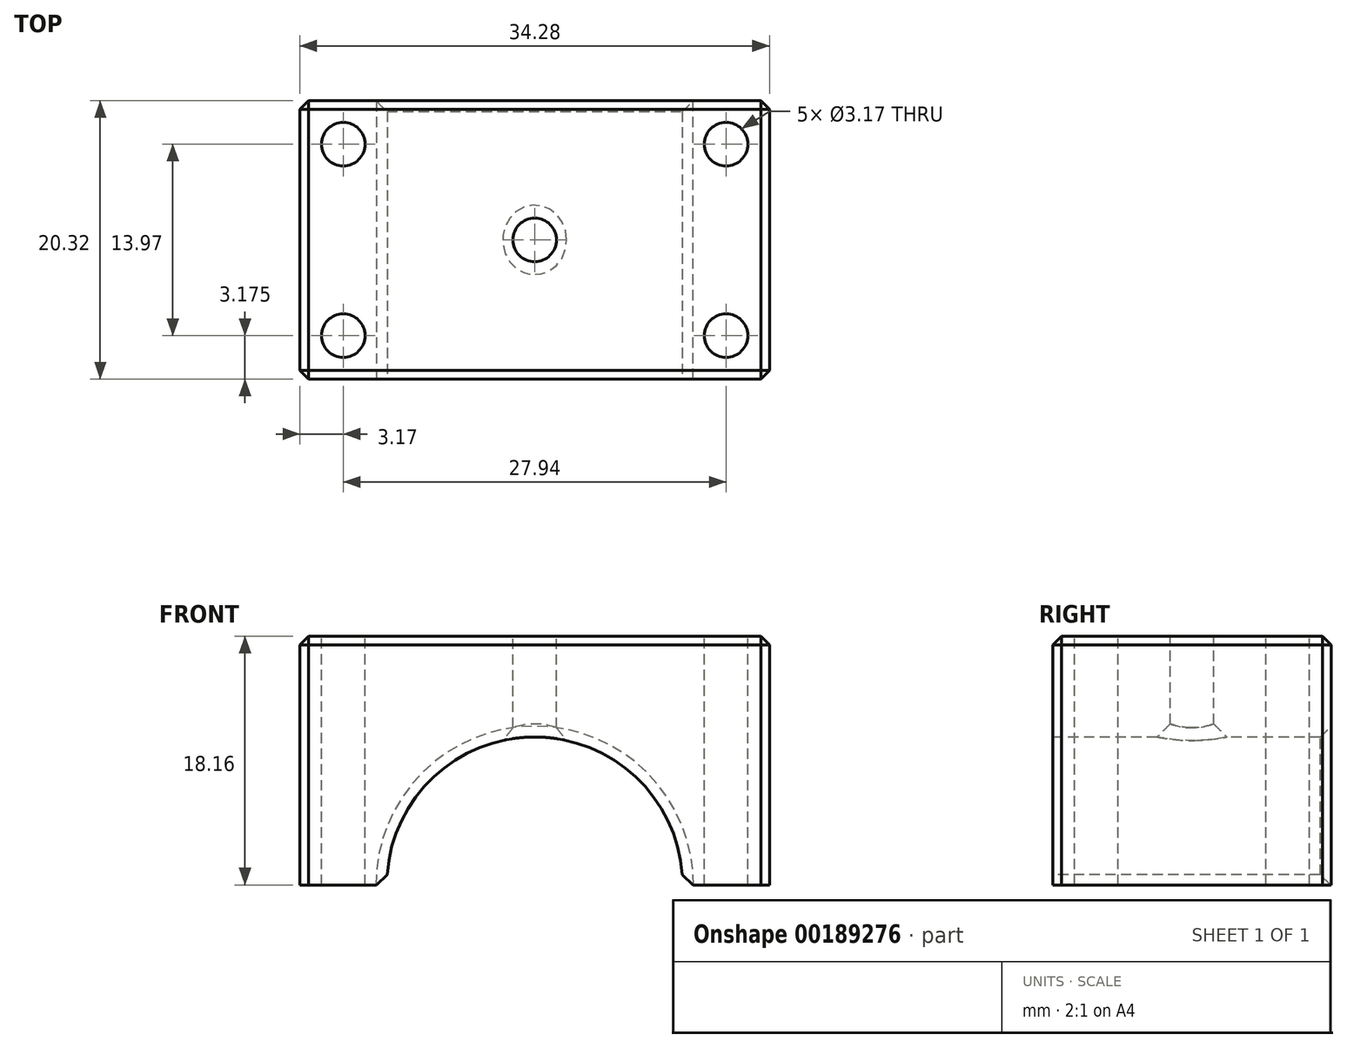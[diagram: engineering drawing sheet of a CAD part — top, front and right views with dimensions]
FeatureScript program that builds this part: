
annotation { "Feature Type Name" : "Feature", "Feature Type Description" : "" }
export const myFeature = defineFeature(function(context is Context, id is Id, definition is map)
    precondition{}
    {
        {
            var Q0;
            Q0=qCreatedBy(makeId("Top.planeOp"),FACE);
            var sketch = newSketch(context, id + "F0", { "sketchPlane" : qUnion([Q0])});
            skLineSegment(sketch, "E0", {"start": v(0, 0) * mm, "end": v(-17.15, 0) * mm});
            skLineSegment(sketch, "E1", {"start": v(-17.15, 0) * mm, "end": v(-17.15, 10.16) * mm});
            skLineSegment(sketch, "E2", {"start": v(-17.15, 10.16) * mm, "end": v(0, 10.16) * mm});
            skLineSegment(sketch, "E3", {"start": v(0, 10.16) * mm, "end": v(0, 0) * mm});
            skLineSegment(sketch, "E4.MirrorCS", {"start": v(17.15, 10.16) * mm, "end": v(0, 10.16) * mm});
            skLineSegment(sketch, "E5.MirrorCS", {"start": v(17.15, 0) * mm, "end": v(17.15, 10.16) * mm});
            skLineSegment(sketch, "E6.MirrorCS", {"start": v(0, 0) * mm, "end": v(17.15, 0) * mm});
            skLineSegment(sketch, "E7.MirrorCS", {"start": v(-17.15, 0) * mm, "end": v(-17.15, -10.16) * mm});
            skLineSegment(sketch, "E8.MirrorCS", {"start": v(-17.15, -10.16) * mm, "end": v(0, -10.16) * mm});
            skLineSegment(sketch, "E9.MirrorCS", {"start": v(17.15, -10.16) * mm, "end": v(0, -10.16) * mm});
            skLineSegment(sketch, "E10.MirrorCS", {"start": v(17.15, 0) * mm, "end": v(17.15, -10.16) * mm});
            skSolve(sketch);
        }
        {
            var Q0;
            Q0 = qSketchRegion(id + "F0", true);
            extrude(context, id + "F1", {"entities" : qUnion([Q0]), "depth" : 18.16 * mm});
        }
        {
            var Q0;
            Q0=makeQuery(id+"F1.opExtrude","SWEPT_FACE",FACE,{"disambiguationData":[OSD([sQuery(id+"F0.wireOp",EDGE,"E8.MirrorCS"),sQuery(id+"F0.wireOp",EDGE,"E9.MirrorCS")])]});
            var sketch = newSketch(context, id + "F2", { "sketchPlane" : qUnion([Q0])});
            skCircle(sketch, "E11", {"center": v(0, 0) * mm, "radius": 10.8 * mm});
            skSolve(sketch);
        }
        {
            var Q0;
            Q0 = qSketchRegion(id + "F2", true);
            extrude(context, id + "F3", {"entities" : qUnion([Q0]), "operationType" : NewBodyOperationType.REMOVE, "oppositeDirection" : true, "depth" : 38.1 * mm});
        }
        {
            var Q0;
            Q0=makeQuery(id+"F1.opExtrude","CAP_FACE",FACE,{"disambiguationData":[OSD([sQuery(id+"F0.wireOp",EDGE,"E1"),sQuery(id+"F0.wireOp",EDGE,"E2"),sQuery(id+"F0.wireOp",EDGE,"E4.MirrorCS"),sQuery(id+"F0.wireOp",EDGE,"E5.MirrorCS"),sQuery(id+"F0.wireOp",EDGE,"E7.MirrorCS"),sQuery(id+"F0.wireOp",EDGE,"E8.MirrorCS"),sQuery(id+"F0.wireOp",EDGE,"E9.MirrorCS"),sQuery(id+"F0.wireOp",EDGE,"E10.MirrorCS")])],"isStart":false});
            var sketch = newSketch(context, id + "F4", { "sketchPlane" : qUnion([Q0])});
            skCircle(sketch, "E12", {"center": v(0, 0) * mm, "radius": 1.59 * mm});
            skCircle(sketch, "E13", {"center": v(13.97, 6.99) * mm, "radius": 1.59 * mm});
            skCircle(sketch, "E14.MirrorC", {"center": v(13.97, -6.99) * mm, "radius": 1.59 * mm});
            skCircle(sketch, "E15.MirrorC", {"center": v(-13.97, 6.99) * mm, "radius": 1.59 * mm});
            skCircle(sketch, "E16.MirrorC", {"center": v(-13.97, -6.99) * mm, "radius": 1.59 * mm});
            skSolve(sketch);
        }
        {
            var Q0;
            Q0 = qSketchRegion(id + "F4", true);
            extrude(context, id + "F5", {"entities" : qUnion([Q0]), "operationType" : NewBodyOperationType.REMOVE, "oppositeDirection" : true, "depth" : 25.4 * mm});
        }
        {
            var Q0;
            Q0=makeQuery(id+"F5.boolean.opBoolean","INTERSECT",EDGE,{"derivedFrom":[makeQuery(id+"F3.boolean.opBoolean","COPY",FACE,{"derivedFrom":makeQuery(id+"F3.opExtrude","SWEPT_FACE",FACE,{"disambiguationData":[OSD([sQuery(id+"F2.wireOp",EDGE,"E11")])]})}),makeQuery(id+"F5.opExtrude","SWEPT_FACE",FACE,{"disambiguationData":[OSD([sQuery(id+"F4.wireOp",EDGE,"E12")])]})]});
            chamfer(context, id + "F6", {"entities" : qUnion([Q0]), "width" : 0.95 * mm, "tangentPropagation" : true});
        }
        {
            var Q0;
            Q0=makeQuery(id+"F3.boolean.opBoolean","INTERSECT",EDGE,{"disambiguationData":[OD(0.0)],"derivedFrom":[makeQuery(id+"F1.opExtrude","CAP_FACE",FACE,{"disambiguationData":[OSD([sQuery(id+"F0.wireOp",EDGE,"E1"),sQuery(id+"F0.wireOp",EDGE,"E2"),sQuery(id+"F0.wireOp",EDGE,"E4.MirrorCS"),sQuery(id+"F0.wireOp",EDGE,"E5.MirrorCS"),sQuery(id+"F0.wireOp",EDGE,"E7.MirrorCS"),sQuery(id+"F0.wireOp",EDGE,"E8.MirrorCS"),sQuery(id+"F0.wireOp",EDGE,"E9.MirrorCS"),sQuery(id+"F0.wireOp",EDGE,"E10.MirrorCS")])],"isStart":true}),makeQuery(id+"F3.opExtrude","SWEPT_FACE",FACE,{"disambiguationData":[OSD([sQuery(id+"F2.wireOp",EDGE,"E11")])]})]});
            var Q1;
            Q1=makeQuery(id+"F3.boolean.opBoolean","INTERSECT",EDGE,{"derivedFrom":[makeQuery(id+"F1.opExtrude","SWEPT_FACE",FACE,{"disambiguationData":[OSD([sQuery(id+"F0.wireOp",EDGE,"E2"),sQuery(id+"F0.wireOp",EDGE,"E4.MirrorCS")])]}),makeQuery(id+"F3.opExtrude","SWEPT_FACE",FACE,{"disambiguationData":[OSD([sQuery(id+"F2.wireOp",EDGE,"E11")])]})]});
            var Q2;
            Q2=makeQuery(id+"F3.boolean.opBoolean","INTERSECT",EDGE,{"disambiguationData":[OD(1.0)],"derivedFrom":[makeQuery(id+"F1.opExtrude","CAP_FACE",FACE,{"disambiguationData":[OSD([sQuery(id+"F0.wireOp",EDGE,"E1"),sQuery(id+"F0.wireOp",EDGE,"E2"),sQuery(id+"F0.wireOp",EDGE,"E4.MirrorCS"),sQuery(id+"F0.wireOp",EDGE,"E5.MirrorCS"),sQuery(id+"F0.wireOp",EDGE,"E7.MirrorCS"),sQuery(id+"F0.wireOp",EDGE,"E8.MirrorCS"),sQuery(id+"F0.wireOp",EDGE,"E9.MirrorCS"),sQuery(id+"F0.wireOp",EDGE,"E10.MirrorCS")])],"isStart":true}),makeQuery(id+"F3.opExtrude","SWEPT_FACE",FACE,{"disambiguationData":[OSD([sQuery(id+"F2.wireOp",EDGE,"E11")])]})]});
            var Q3;
            Q3=makeQuery(id+"F3.boolean.opBoolean","COPY",EDGE,{"derivedFrom":makeQuery(id+"F3.opExtrude","CAP_EDGE",EDGE,{"disambiguationData":[OSD([sQuery(id+"F2.wireOp",EDGE,"E11")])],"isStart":true})});
            chamfer(context, id + "F7", {"entities" : qUnion([Q0, Q1, Q2, Q3]), "width" : 0.8 * mm, "tangentPropagation" : true});
        }
        {
            var Q0;
            Q0=makeQuery(id+"F1.opExtrude","SWEPT_EDGE",EDGE,{"disambiguationData":[OSD([sQuery(id+"F0.wireOp",EDGE,"E9.MirrorCS"),sQuery(id+"F0.wireOp",EDGE,"E10.MirrorCS")])]});
            var Q1;
            Q1=makeQuery(id+"F1.opExtrude","SWEPT_EDGE",EDGE,{"disambiguationData":[OSD([sQuery(id+"F0.wireOp",EDGE,"E7.MirrorCS"),sQuery(id+"F0.wireOp",EDGE,"E8.MirrorCS")])]});
            var Q2;
            Q2=makeQuery(id+"F1.opExtrude","SWEPT_EDGE",EDGE,{"disambiguationData":[OSD([sQuery(id+"F0.wireOp",EDGE,"E1"),sQuery(id+"F0.wireOp",EDGE,"E2")])]});
            var Q3;
            Q3=makeQuery(id+"F1.opExtrude","SWEPT_EDGE",EDGE,{"disambiguationData":[OSD([sQuery(id+"F0.wireOp",EDGE,"E4.MirrorCS"),sQuery(id+"F0.wireOp",EDGE,"E5.MirrorCS")])]});
            var Q4;
            Q4=makeQuery(id+"F1.opExtrude","CAP_EDGE",EDGE,{"disambiguationData":[OSD([sQuery(id+"F0.wireOp",EDGE,"E2"),sQuery(id+"F0.wireOp",EDGE,"E4.MirrorCS")])],"isStart":false});
            var Q5;
            Q5=makeQuery(id+"F1.opExtrude","CAP_EDGE",EDGE,{"disambiguationData":[OSD([sQuery(id+"F0.wireOp",EDGE,"E8.MirrorCS"),sQuery(id+"F0.wireOp",EDGE,"E9.MirrorCS")])],"isStart":false});
            var Q6;
            Q6=makeQuery(id+"F1.opExtrude","CAP_EDGE",EDGE,{"disambiguationData":[OSD([sQuery(id+"F0.wireOp",EDGE,"E1"),sQuery(id+"F0.wireOp",EDGE,"E7.MirrorCS")])],"isStart":false});
            var Q7;
            Q7=makeQuery(id+"F1.opExtrude","CAP_EDGE",EDGE,{"disambiguationData":[OSD([sQuery(id+"F0.wireOp",EDGE,"E5.MirrorCS"),sQuery(id+"F0.wireOp",EDGE,"E10.MirrorCS")])],"isStart":false});
            chamfer(context, id + "F8", {"entities" : qUnion([Q0, Q1, Q2, Q3, Q4, Q5, Q6, Q7]), "width" : 0.64 * mm, "tangentPropagation" : true});
        }
    });
